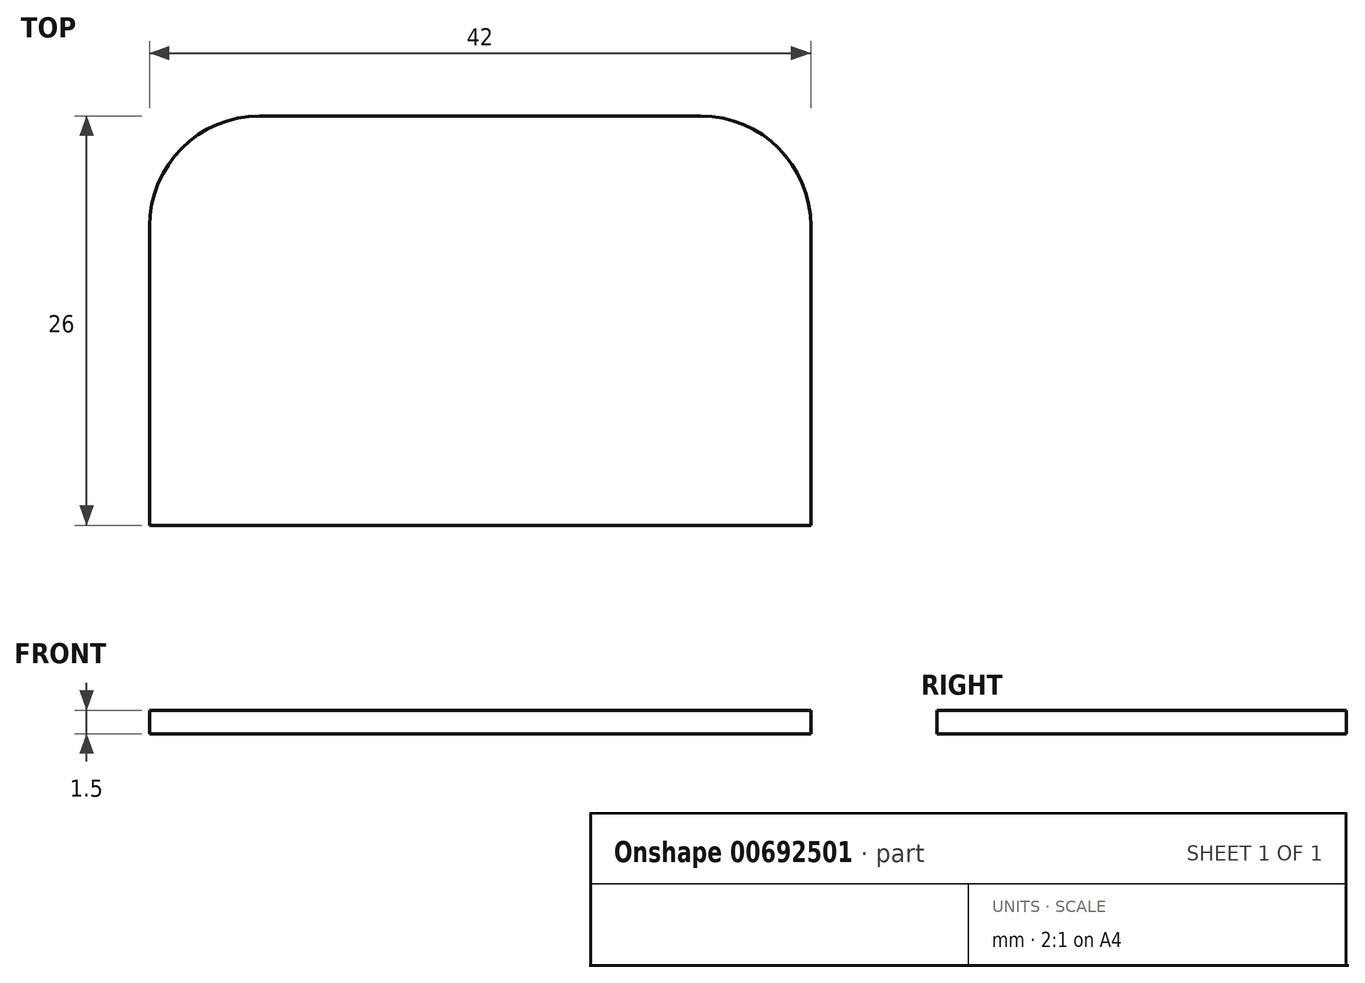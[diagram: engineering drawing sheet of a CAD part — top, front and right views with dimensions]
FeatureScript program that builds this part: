
annotation { "Feature Type Name" : "Feature", "Feature Type Description" : "" }
export const myFeature = defineFeature(function(context is Context, id is Id, definition is map)
    precondition{}
    {
        {
            var Q0;
            Q0=qCreatedBy(makeId("Top.planeOp"),FACE);
            var sketch = newSketch(context, id + "F0", { "sketchPlane" : qUnion([Q0])});
            skLineSegment(sketch, "E0.bottom", {"start": v(0, 0) * mm, "end": v(42, 0) * mm});
            skLineSegment(sketch, "E0.top", {"start": v(7, 26) * mm, "end": v(35, 26) * mm});
            skLineSegment(sketch, "E0.left", {"start": v(0, 0) * mm, "end": v(0, 19) * mm});
            skLineSegment(sketch, "E0.right", {"start": v(42, 0) * mm, "end": v(42, 19) * mm});
            skPoint(sketch, "E1.visualSharp", {"position": v(42, 26) * mm});
            skArc(sketch, "E1.filletArc", {"start": v(42, 19) * mm, "mid": v(39.95, 23.95) * mm, "end": v(35, 26) * mm});
            skPoint(sketch, "E2.visualSharp", {"position": v(0, 26) * mm});
            skArc(sketch, "E2.filletArc", {"start": v(7, 26) * mm, "mid": v(2.05, 23.95) * mm, "end": v(0, 19) * mm});
            skSolve(sketch);
        }
        {
            var Q0;
            Q0 = qSketchRegion(id + "F0", true);
            extrude(context, id + "F1", {"entities" : qUnion([Q0]), "depth" : 1.5 * mm, "offsetDistance" : 25 * mm});
        }
    });
